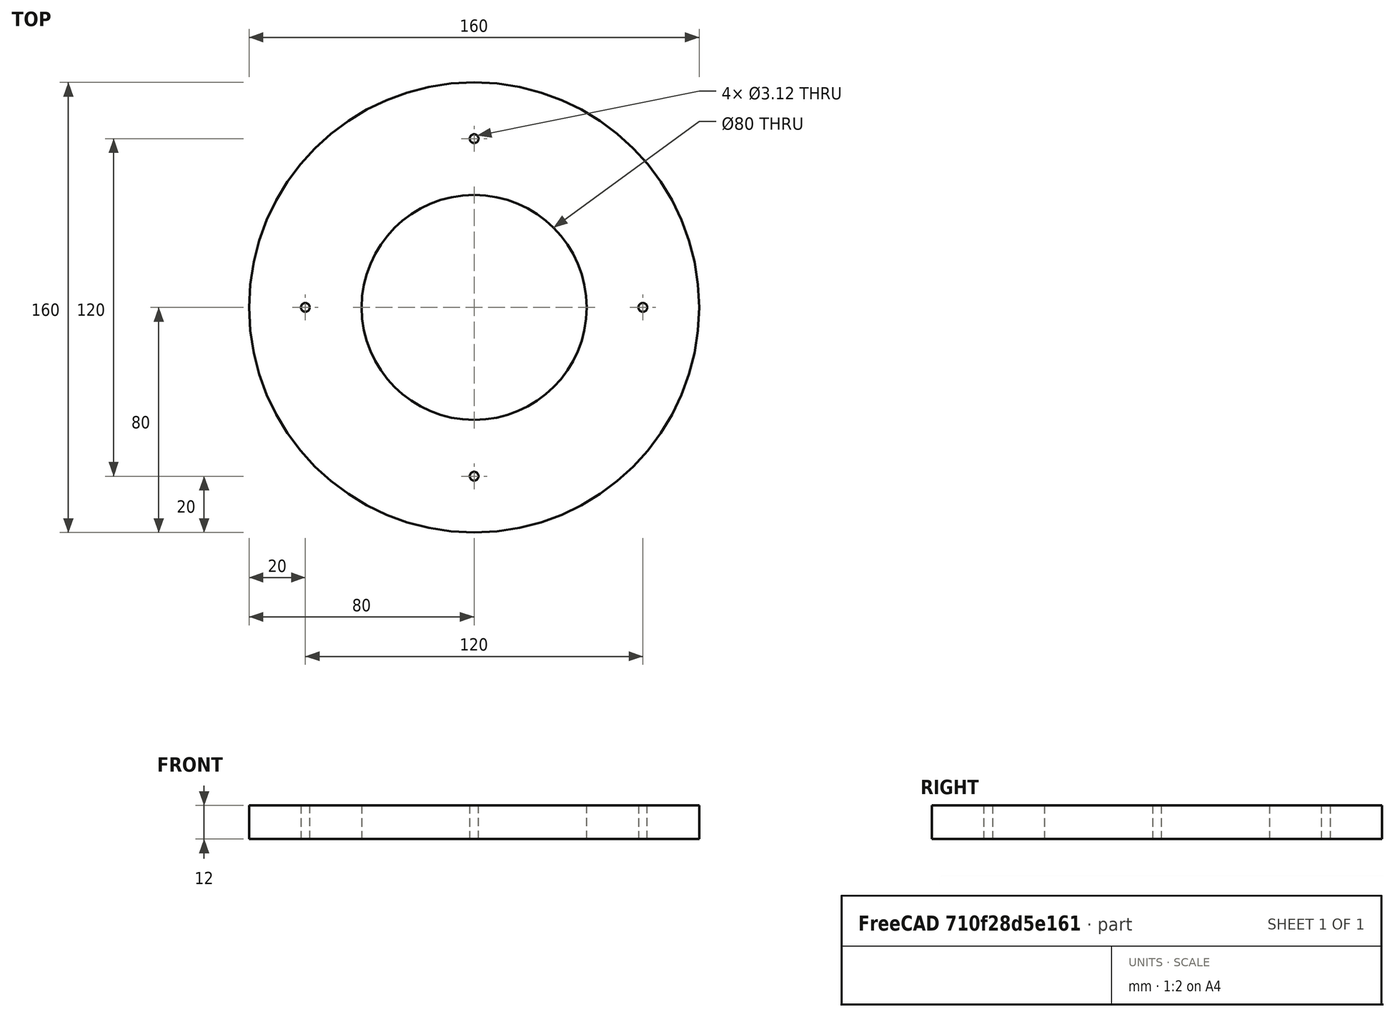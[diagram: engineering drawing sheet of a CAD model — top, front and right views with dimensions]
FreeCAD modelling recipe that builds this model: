
FCSTD DOCUMENT  (FreeCAD 0.19R24276 (Git))
Label: Out_gear_holder_for_CNC_Under_bottom_part_H12
License: All rights reserved
LicenseURL: http://en.wikipedia.org/wiki/All_rights_reserved
objects: Sketcher::SketchObject×1, PartDesign::Pad×1, PartDesign::Body×1
note: 4 computed .brp shape members not serialized (recipe doc carries the construction recipe); baked Part::Feature solids carry a one-line shape summary decoded from their .brp

FEATURE [Sketcher::SketchObject] Sketch  label="_d80_d160"
  FullyConstrained = true
  MapMode = 5
  Support = -> [XY_Plane]
  sketch-geometry (12):
    g0: Circle CenterX=0 CenterY=0 CenterZ=0 NormalX=0 NormalY=0 NormalZ=1 AngleXU=0 Radius=40
    g1: Circle CenterX=0 CenterY=0 CenterZ=0 NormalX=0 NormalY=0 NormalZ=1 AngleXU=0 Radius=80
    g2: LineSegment StartX=0 StartY=60 StartZ=0 EndX=-60 EndY=-1.42e-14 EndZ=0
    g3: LineSegment StartX=-60 StartY=-1.42e-14 StartZ=0 EndX=-7.1e-15 EndY=-60 EndZ=0
    g4: LineSegment StartX=-7.1e-15 StartY=-60 StartZ=0 EndX=60 EndY=0 EndZ=0
    g5: LineSegment StartX=60 StartY=0 StartZ=0 EndX=0 EndY=60 EndZ=0
    g6: Circle CenterX=0 CenterY=0 CenterZ=0 NormalX=0 NormalY=0 NormalZ=1 AngleXU=0 Radius=60
    g7: Circle CenterX=0 CenterY=60 CenterZ=0 NormalX=0 NormalY=0 NormalZ=1 AngleXU=0 Radius=1.5625
    g8: Circle CenterX=-60 CenterY=-1.42e-14 CenterZ=0 NormalX=0 NormalY=0 NormalZ=1 AngleXU=0 Radius=1.5625
    g9: Circle CenterX=-7.1e-15 CenterY=-60 CenterZ=0 NormalX=0 NormalY=0 NormalZ=1 AngleXU=0 Radius=1.5625
    g10: Circle CenterX=60 CenterY=0 CenterZ=0 NormalX=0 NormalY=0 NormalZ=1 AngleXU=0 Radius=1.8e-15
    g11: Circle CenterX=60 CenterY=0 CenterZ=0 NormalX=0 NormalY=0 NormalZ=1 AngleXU=0 Radius=1.5625
  constraints (28):
    c: Coincident(g0,g-1)
    c: Diameter(g0) = 80
    c: Coincident(g1,g0)
    c: Diameter(g1) = 160
    c: Coincident(g2,g3)
    c: Coincident(g3,g4)
    c: Coincident(g4,g5)
    c: Coincident(g5,g2)
    c: Equal(g2,g3)
    c: Equal(g2,g4)
    c: Equal(g2,g5)
    c: PointOnObject(g2,g6)
    c: PointOnObject(g3,g6)
    c: PointOnObject(g4,g6)
    c: PointOnObject(g5,g6)
    c: Coincident(g6,g0)
    c: PointOnObject(g5,g-2)
    c: Diameter(g6) = 120
    c: Coincident(g7,g2)
    c: Coincident(g8,g2)
    c: Coincident(g9,g3)
    c: Coincident(g10,g4)
    c: Tangent(g10,g6)
    c: Coincident(g11,g10)
    c: Diameter(g7) = 3.125
    c: Equal(g7,g8)
    c: Equal(g7,g9)
    c: Equal(g7,g11)
FEATURE [PartDesign::Pad] Pad  label="Pad_h12"
  Direction = (1,1,1)
  Length = 12
  Length2 = 100
  Profile = -> Sketch
  Type = 0
FEATURE [PartDesign::Body] Body
  Group = -> [Sketch,Pad]
  Origin = -> Origin
  Tip = -> Pad
